# Revit family: 3-535-xx - 37-535-xx - Halo (Wall Sconce)
name_source: partatom
category: Lighting Fixtures
revit_build: Autodesk Revit 2018 (Build: 20180423_1000(x64)
units: mm (PartAtom-declared; Revit-internal decimal feet)

## family parameters
Cut with Voids When Loaded = No
Host = Face
Light Source = Yes
Part Type = Normal
Room Calculation Point = No
Round Connector Dimension = Use Diameter
Shared = No

## types (4) — shared parameters
2nd Diffuser = <By Category>
Color Filter = 16777215
Dimming Lamp Color Temperature Shift = <None>
Emit Shape Visible in Rendering = No
Emit from Rectangle Length = 11 "
Emit from Rectangle Width = 1 "
Lamp = LED Array
Main Diffuser = Matte White Acrylic
Manufacturer = Oxygen Lighting & Fans
Model = 3-535-XX / 37-535-XX - Halo
Other 1 = <By Category>
Other 2 = <By Category>
Photometric Web File = 3-535-xx Halo Sconce.ies
Tilt Angle = 180.00°
URL = www.oxygenlighting.com
Wattage Comments = 13.0 W at 120 V
zero-valued in all types: Default Elevation

## per-type parameters (varying)
| type | Metal Finish |
| 3-535-14 / 37-535-14 - Halo | 14 - Polished Chrome |
| 3-535-24 / 37-535-24 - Halo | 24 - Satin Nickel |
| 3-535-25 / 37-535-25 - Halo | 25 - Satin Copper |
| 3-535-40 / 37-535-40 - Halo | 40 - Aged Brass |

## geometry (parser evidence)
native form markers: Extrusion x1, Sweep x5
no freeform markers — native parametric forms only
